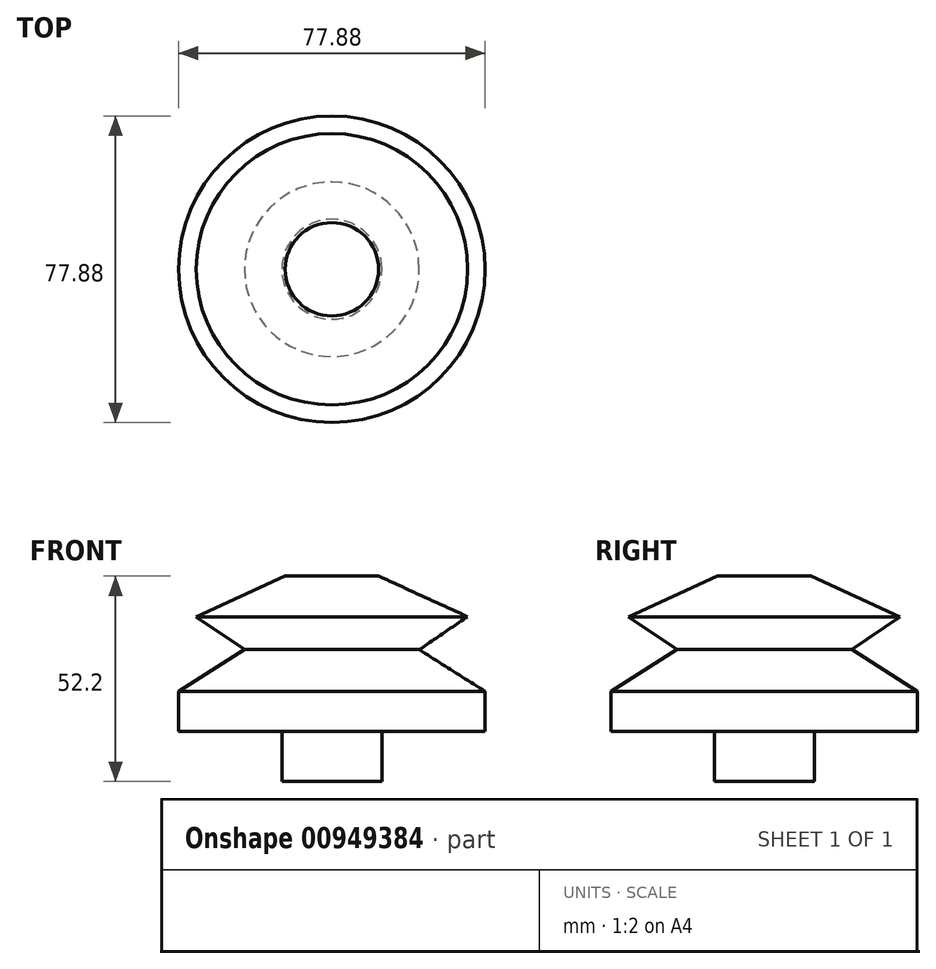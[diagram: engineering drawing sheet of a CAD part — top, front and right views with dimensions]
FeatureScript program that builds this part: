
annotation { "Feature Type Name" : "Feature", "Feature Type Description" : "" }
export const myFeature = defineFeature(function(context is Context, id is Id, definition is map)
    precondition{}
    {
        {
            var Q0;
            Q0=qCreatedBy(makeId("Front.planeOp"),FACE);
            var sketch = newSketch(context, id + "F0", { "sketchPlane" : qUnion([Q0])});
            skLineSegment(sketch, "E0", {"start": v(11.86, 52.2) * mm, "end": v(34.47, 41.87) * mm});
            skLineSegment(sketch, "E1", {"start": v(34.47, 41.87) * mm, "end": v(22.2, 33.5) * mm});
            skLineSegment(sketch, "E2", {"start": v(22.2, 33.5) * mm, "end": v(38.94, 22.89) * mm});
            skLineSegment(sketch, "E3", {"start": v(38.94, 22.89) * mm, "end": v(38.94, 12.7) * mm});
            skLineSegment(sketch, "E4", {"start": v(38.94, 12.7) * mm, "end": v(12.7, 12.7) * mm});
            skLineSegment(sketch, "E5", {"start": v(12.7, 12.7) * mm, "end": v(12.7, 0) * mm});
            skLineSegment(sketch, "E6", {"start": v(12.7, 0) * mm, "end": v(0, 0) * mm});
            skLineSegment(sketch, "E7", {"start": v(0, 0) * mm, "end": v(0, 52.2) * mm});
            skLineSegment(sketch, "E8", {"start": v(0, 52.2) * mm, "end": v(11.86, 52.2) * mm});
            skLineSegment(sketch, "E9", {"start": v(0, 65.98) * mm, "end": v(0, -54.11) * mm, "construction": true});
            skSolve(sketch);
        }
        {
            var Q0;
            Q0 = qSketchRegion(id + "F0", true);
            var Q1;
            Q1=sQuery(id+"F0.wireOp",EDGE,"E9");
            revolve(context, id + "F1", {"surfaceOperationType" : NewSurfaceOperationType.NEW, "entities" : qUnion([Q0]), "axis" : qUnion([Q1]), "revolveType" : RevolveType.FULL});
        }
    });
